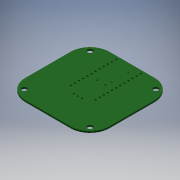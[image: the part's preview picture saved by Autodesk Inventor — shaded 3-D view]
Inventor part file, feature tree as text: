
AUTODESK INVENTOR PART (.ipt)
format: ipt  version: 2018 (Build 220112000, 112)  size: 185,856 bytes
history: native  units: mm
features: extrude x1, sketch x1, projected_geometry x1, imported_body x1
ambient origin geometry x8: Origin, YZ Plane, XZ Plane, XY Plane, X Axis, Y Axis, Z Axis, Center Point
bodies: Volumenkörper1 (feature_tree)
feature tree (4):
  extrude  "Extrusion1"  [1 undecoded]
  sketch  "Skizze1"  dims[d0=0.6mm d1=0.0mm]
  projected_geometry  "Projizierte Kontur1"
  imported_body  "Basis1"
note: 1 required parameter value undecoded (feature->parameter linkage not recoverable at this tier; creation-order binding heuristic only, values carry confidence <= 0.55)
